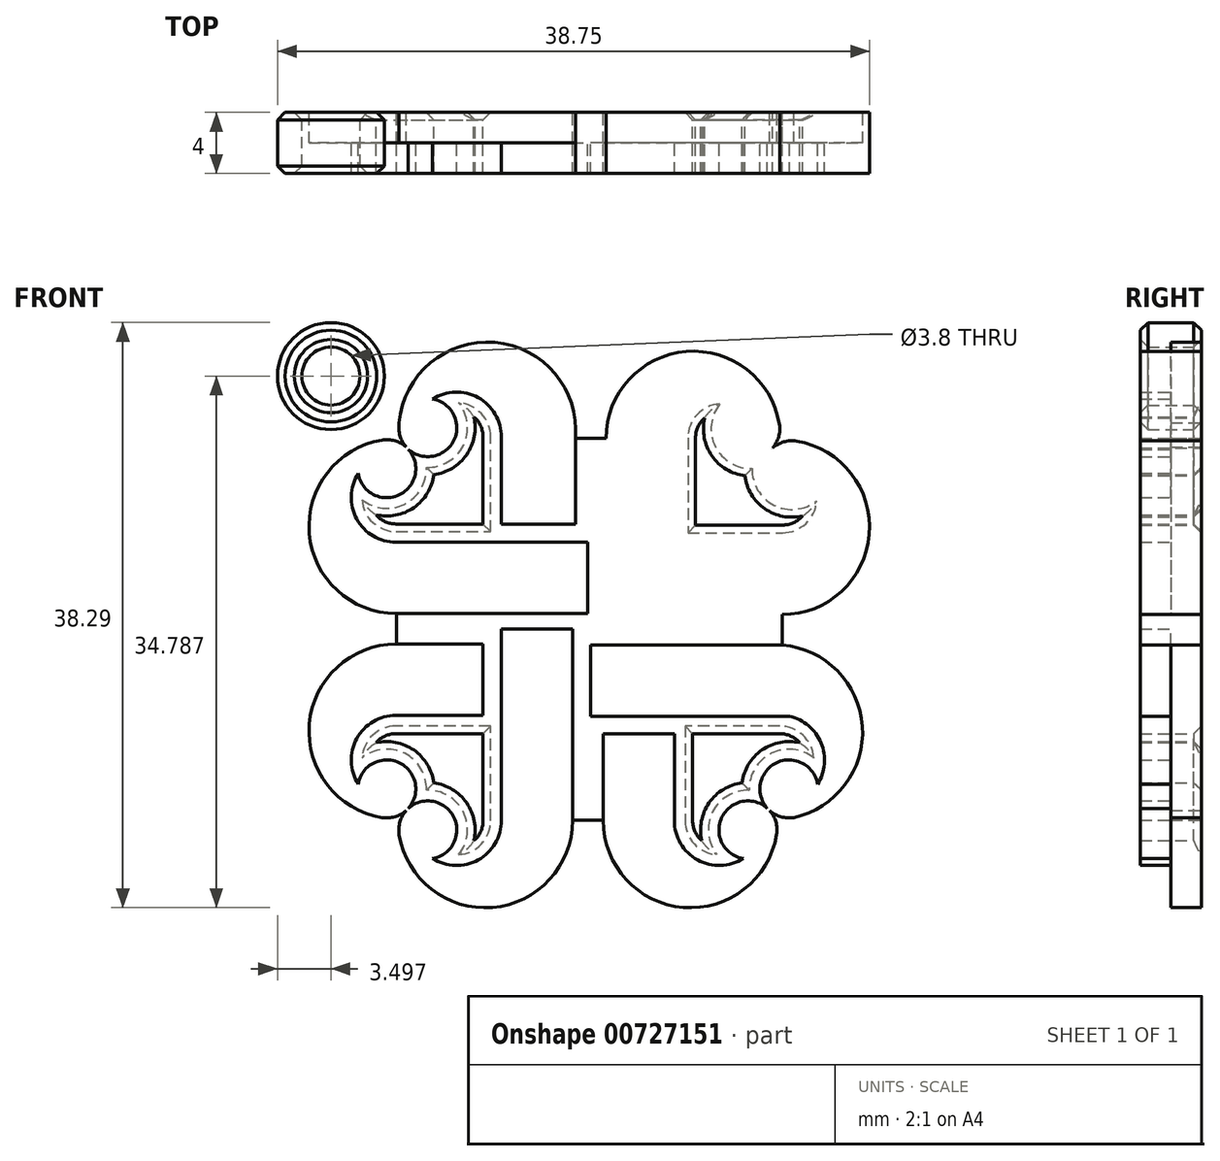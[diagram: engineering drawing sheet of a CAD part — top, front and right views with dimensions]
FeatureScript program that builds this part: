
annotation { "Feature Type Name" : "Feature", "Feature Type Description" : "" }
export const myFeature = defineFeature(function(context is Context, id is Id, definition is map)
    precondition{}
    {
        {
            var Q0;
            Q0=qCreatedBy(makeId("Front.planeOp"),FACE);
            var sketch = newSketch(context, id + "F0", { "sketchPlane" : qUnion([Q0])});
            skPoint(sketch, "E0.middle", {"position": v(0, 0) * mm});
            skLineSegment(sketch, "E1.0", {"start": v(1.19, 12.45) * mm, "end": v(1.19, 0.91) * mm});
            skLineSegment(sketch, "E2.MirrorCS", {"start": v(5.84, 12.48) * mm, "end": v(5.84, -0.09) * mm});
            skArc(sketch, "E3.MirrorCS", {"start": v(5.84, 12.48) * mm, "mid": v(7.36, 15.05) * mm, "end": v(10.35, 14.96) * mm});
            skArc(sketch, "E4.MirrorCS", {"start": v(12.53, 13.4) * mm, "mid": v(12.48, 12.56) * mm, "end": v(12.07, 11.82) * mm});
            skArc(sketch, "E5.MirrorCS", {"start": v(1.19, 12.45) * mm, "mid": v(6.43, 18.14) * mm, "end": v(12.53, 13.4) * mm});
            skPoint(sketch, "E6.MirrorP", {"position": v(8.93, 15.5) * mm});
            skPoint(sketch, "E7.MirrorP", {"position": v(12.53, 13.4) * mm});
            skPoint(sketch, "E8.MirrorP", {"position": v(10.35, 14.96) * mm});
            skLineSegment(sketch, "E9.0", {"start": v(7.04, 12.48) * mm, "end": v(7.04, 6.79) * mm});
            skArc(sketch, "E9.1", {"start": v(7.04, 12.48) * mm, "mid": v(7.2, 13.2) * mm, "end": v(7.64, 13.8) * mm});
            skArc(sketch, "E9.3", {"start": v(1.1, 16.21) * mm, "mid": v(8.05, 19.27) * mm, "end": v(13.61, 14.1) * mm});
            skLineSegment(sketch, "E10.MirrorCS", {"start": v(12.72, 0.93) * mm, "end": v(7.04, 0.93) * mm});
            skLineSegment(sketch, "E11.MirrorCS", {"start": v(12.74, 5.59) * mm, "end": v(7.04, 5.59) * mm});
            skLineSegment(sketch, "E12.MirrorCS", {"start": v(12.74, 6.79) * mm, "end": v(7.04, 6.79) * mm});
            skPoint(sketch, "E13.MirrorP", {"position": v(15.5, 8.93) * mm});
            skPoint(sketch, "E14.MirrorP", {"position": v(15.22, 10.1) * mm});
            skArc(sketch, "E15.MirrorCS", {"start": v(12.72, 0.93) * mm, "mid": v(18.42, 6.17) * mm, "end": v(13.66, 12.28) * mm});
            skArc(sketch, "E16.MirrorCS", {"start": v(12.74, 5.59) * mm, "mid": v(15.31, 7.1) * mm, "end": v(15.22, 10.1) * mm});
            skArc(sketch, "E17.MirrorCS", {"start": v(12.74, 6.79) * mm, "mid": v(13.46, 6.94) * mm, "end": v(14.05, 7.39) * mm});
            skPoint(sketch, "E18.MirrorP", {"position": v(13.66, 12.28) * mm});
            skArc(sketch, "E19.MirrorCS", {"start": v(16.38, 0.78) * mm, "mid": v(19.55, 7.74) * mm, "end": v(14.35, 13.36) * mm});
            skArc(sketch, "E20.MirrorCS", {"start": v(13.66, 12.28) * mm, "mid": v(12.81, 12.23) * mm, "end": v(12.08, 11.82) * mm});
            skArc(sketch, "E21.trimOffspring", {"start": v(10.27, 10.02) * mm, "mid": v(8.12, 11.32) * mm, "end": v(7.64, 13.8) * mm});
            skArc(sketch, "E22.trimOffspring", {"start": v(10.27, 10.02) * mm, "mid": v(11.58, 7.86) * mm, "end": v(14.05, 7.39) * mm});
            skLineSegment(sketch, "E23.1.0", {"start": v(-12.55, 5.66) * mm, "end": v(0, 5.66) * mm});
            skArc(sketch, "E23.1.1", {"start": v(-13.47, 12.35) * mm, "mid": v(-12.63, 12.3) * mm, "end": v(-11.9, 11.89) * mm});
            skPoint(sketch, "E23.1.2", {"position": v(-13.47, 12.35) * mm});
            skArc(sketch, "E23.1.3", {"start": v(-10.09, 10.09) * mm, "mid": v(-7.93, 11.4) * mm, "end": v(-7.46, 13.87) * mm});
            skPoint(sketch, "E23.1.4", {"position": v(-15.03, 10.17) * mm});
            skLineSegment(sketch, "E23.1.5", {"start": v(-6.86, 12.55) * mm, "end": v(-6.86, 6.86) * mm});
            skArc(sketch, "E23.1.6", {"start": v(-0.6, 16.26) * mm, "mid": v(-7.9, 19.82) * mm, "end": v(-13.84, 14.32) * mm});
            skArc(sketch, "E23.1.7", {"start": v(-0.81, 12.47) * mm, "mid": v(-6.08, 18.74) * mm, "end": v(-12.35, 13.47) * mm});
            skLineSegment(sketch, "E23.1.9", {"start": v(-5.66, 12.55) * mm, "end": v(-5.66, 6.86) * mm});
            skPoint(sketch, "E23.1.10", {"position": v(-15.5, 8.93) * mm});
            skArc(sketch, "E23.1.11", {"start": v(-12.54, 1) * mm, "mid": v(-18.23, 6.24) * mm, "end": v(-13.47, 12.35) * mm});
            skArc(sketch, "E23.1.12", {"start": v(-10.09, 10.09) * mm, "mid": v(-11.4, 7.93) * mm, "end": v(-13.87, 7.46) * mm});
            skArc(sketch, "E23.1.13", {"start": v(-12.35, 13.47) * mm, "mid": v(-12.3, 12.63) * mm, "end": v(-11.89, 11.9) * mm});
            skArc(sketch, "E23.1.14", {"start": v(-16.76, 0.1) * mm, "mid": v(-20.22, 7.56) * mm, "end": v(-14.6, 13.56) * mm});
            skLineSegment(sketch, "E23.1.15", {"start": v(-12.54, 1) * mm, "end": v(-1, 1) * mm});
            skLineSegment(sketch, "E23.1.16", {"start": v(-0.81, 12.47) * mm, "end": v(-0.81, 6.86) * mm});
            skPoint(sketch, "E23.1.17", {"position": v(-8.93, 15.5) * mm});
            skPoint(sketch, "E23.1.18", {"position": v(-10.17, 15.03) * mm});
            skPoint(sketch, "E23.1.19", {"position": v(-12.35, 13.47) * mm});
            skArc(sketch, "E23.1.20", {"start": v(-12.55, 5.66) * mm, "mid": v(-15.12, 7.18) * mm, "end": v(-15.03, 10.17) * mm});
            skArc(sketch, "E23.1.21", {"start": v(-12.55, 6.86) * mm, "mid": v(-13.27, 7.02) * mm, "end": v(-13.87, 7.46) * mm});
            skLineSegment(sketch, "E23.1.22", {"start": v(-12.55, 6.86) * mm, "end": v(-6.86, 6.86) * mm});
            skArc(sketch, "E23.1.23", {"start": v(-6.86, 12.55) * mm, "mid": v(-7.02, 13.27) * mm, "end": v(-7.46, 13.87) * mm});
            skArc(sketch, "E23.1.24", {"start": v(-5.66, 12.55) * mm, "mid": v(-7.18, 15.12) * mm, "end": v(-10.17, 15.03) * mm});
            skLineSegment(sketch, "E23.1.25", {"start": v(-12.54, 1) * mm, "end": v(-1, 1) * mm});
            skLineSegment(sketch, "E23.2.0", {"start": v(-5.66, -12.55) * mm, "end": v(-5.66, 0) * mm});
            skArc(sketch, "E23.2.1", {"start": v(-12.35, -13.47) * mm, "mid": v(-12.3, -12.63) * mm, "end": v(-11.89, -11.9) * mm});
            skPoint(sketch, "E23.2.2", {"position": v(-12.35, -13.47) * mm});
            skArc(sketch, "E23.2.3", {"start": v(-10.09, -10.09) * mm, "mid": v(-11.4, -7.93) * mm, "end": v(-13.87, -7.46) * mm});
            skPoint(sketch, "E23.2.4", {"position": v(-10.17, -15.03) * mm});
            skLineSegment(sketch, "E23.2.5", {"start": v(-12.55, -6.86) * mm, "end": v(-6.86, -6.86) * mm});
            skArc(sketch, "E23.2.6", {"start": v(-16.72, -1.58) * mm, "mid": v(-19.62, -8.36) * mm, "end": v(-14.59, -13.75) * mm});
            skArc(sketch, "E23.2.7", {"start": v(-12.54, -1) * mm, "mid": v(-18.23, -6.24) * mm, "end": v(-13.47, -12.35) * mm});
            skLineSegment(sketch, "E23.2.9", {"start": v(-12.55, -5.66) * mm, "end": v(-6.86, -5.66) * mm});
            skPoint(sketch, "E23.2.10", {"position": v(-8.93, -15.5) * mm});
            skArc(sketch, "E23.2.11", {"start": v(-1, -12.54) * mm, "mid": v(-6.24, -18.23) * mm, "end": v(-12.35, -13.47) * mm});
            skArc(sketch, "E23.2.12", {"start": v(-10.09, -10.09) * mm, "mid": v(-7.93, -11.4) * mm, "end": v(-7.46, -13.87) * mm});
            skArc(sketch, "E23.2.13", {"start": v(-13.47, -12.35) * mm, "mid": v(-12.63, -12.3) * mm, "end": v(-11.9, -11.89) * mm});
            skArc(sketch, "E23.2.14", {"start": v(-1.27, -16.52) * mm, "mid": v(-8.24, -19.68) * mm, "end": v(-13.85, -14.49) * mm});
            skLineSegment(sketch, "E23.2.15", {"start": v(-1, -12.54) * mm, "end": v(-1, -1) * mm});
            skLineSegment(sketch, "E23.2.16", {"start": v(-12.54, -1) * mm, "end": v(-6.86, -1) * mm});
            skPoint(sketch, "E23.2.17", {"position": v(-15.5, -8.93) * mm});
            skPoint(sketch, "E23.2.18", {"position": v(-15.03, -10.17) * mm});
            skPoint(sketch, "E23.2.19", {"position": v(-13.47, -12.35) * mm});
            skArc(sketch, "E23.2.20", {"start": v(-5.66, -12.55) * mm, "mid": v(-7.18, -15.12) * mm, "end": v(-10.17, -15.03) * mm});
            skArc(sketch, "E23.2.21", {"start": v(-6.86, -12.55) * mm, "mid": v(-7.02, -13.27) * mm, "end": v(-7.46, -13.87) * mm});
            skLineSegment(sketch, "E23.2.22", {"start": v(-6.86, -12.55) * mm, "end": v(-6.86, -6.86) * mm});
            skArc(sketch, "E23.2.23", {"start": v(-12.55, -6.86) * mm, "mid": v(-13.27, -7.02) * mm, "end": v(-13.87, -7.46) * mm});
            skArc(sketch, "E23.2.24", {"start": v(-12.55, -5.66) * mm, "mid": v(-15.12, -7.18) * mm, "end": v(-15.03, -10.17) * mm});
            skLineSegment(sketch, "E23.2.25", {"start": v(-1, -12.54) * mm, "end": v(-1, -1) * mm});
            skLineSegment(sketch, "E23.3.0", {"start": v(13.2, -5.73) * mm, "end": v(0.19, -5.73) * mm});
            skArc(sketch, "E23.3.1", {"start": v(13.47, -12.35) * mm, "mid": v(12.63, -12.3) * mm, "end": v(11.9, -11.89) * mm});
            skPoint(sketch, "E23.3.2", {"position": v(13.47, -12.35) * mm});
            skArc(sketch, "E23.3.3", {"start": v(10.09, -10.09) * mm, "mid": v(7.93, -11.4) * mm, "end": v(7.46, -13.87) * mm});
            skPoint(sketch, "E23.3.4", {"position": v(15.03, -10.17) * mm});
            skLineSegment(sketch, "E23.3.5", {"start": v(6.86, -12.55) * mm, "end": v(6.86, -6.86) * mm});
            skArc(sketch, "E23.3.6", {"start": v(0.42, -16.52) * mm, "mid": v(7.45, -19.67) * mm, "end": v(13.03, -14.37) * mm});
            skArc(sketch, "E23.3.7", {"start": v(1, -12.54) * mm, "mid": v(6.24, -18.23) * mm, "end": v(12.35, -13.47) * mm});
            skLineSegment(sketch, "E23.3.9", {"start": v(5.66, -12.55) * mm, "end": v(5.66, -6.86) * mm});
            skPoint(sketch, "E23.3.10", {"position": v(15.5, -8.93) * mm});
            skArc(sketch, "E23.3.11", {"start": v(12.72, -1.07) * mm, "mid": v(17.96, -6.39) * mm, "end": v(13.47, -12.35) * mm});
            skArc(sketch, "E23.3.12", {"start": v(10.09, -10.09) * mm, "mid": v(11.4, -7.93) * mm, "end": v(13.87, -7.46) * mm});
            skArc(sketch, "E23.3.13", {"start": v(12.35, -13.47) * mm, "mid": v(12.3, -12.63) * mm, "end": v(11.89, -11.9) * mm});
            skArc(sketch, "E23.3.14", {"start": v(16.38, -0.92) * mm, "mid": v(19.5, -8.14) * mm, "end": v(13.85, -13.6) * mm});
            skLineSegment(sketch, "E23.3.15", {"start": v(12.72, -1.07) * mm, "end": v(1.19, -1.07) * mm});
            skLineSegment(sketch, "E23.3.16", {"start": v(1, -12.54) * mm, "end": v(1, -6.86) * mm});
            skPoint(sketch, "E23.3.17", {"position": v(8.93, -15.5) * mm});
            skPoint(sketch, "E23.3.18", {"position": v(10.17, -15.03) * mm});
            skPoint(sketch, "E23.3.19", {"position": v(12.35, -13.47) * mm});
            skArc(sketch, "E23.3.20", {"start": v(13.2, -5.73) * mm, "mid": v(15.26, -7.47) * mm, "end": v(15.03, -10.17) * mm});
            skArc(sketch, "E23.3.21", {"start": v(12.55, -6.86) * mm, "mid": v(13.27, -7.02) * mm, "end": v(13.87, -7.46) * mm});
            skLineSegment(sketch, "E23.3.22", {"start": v(12.55, -6.86) * mm, "end": v(6.86, -6.86) * mm});
            skArc(sketch, "E23.3.23", {"start": v(6.86, -12.55) * mm, "mid": v(7.02, -13.27) * mm, "end": v(7.46, -13.87) * mm});
            skArc(sketch, "E23.3.24", {"start": v(5.66, -12.55) * mm, "mid": v(7.18, -15.12) * mm, "end": v(10.17, -15.03) * mm});
            skLineSegment(sketch, "E23.3.25", {"start": v(12.72, -1.07) * mm, "end": v(1.19, -1.07) * mm});
            skLineSegment(sketch, "E24", {"start": v(5.84, -0.09) * mm, "end": v(1.19, -0.09) * mm});
            skLineSegment(sketch, "E25", {"start": v(0, 5.66) * mm, "end": v(0, 1) * mm});
            skLineSegment(sketch, "E26", {"start": v(-5.66, 0) * mm, "end": v(-1, 0) * mm});
            skLineSegment(sketch, "E27", {"start": v(0.19, -5.73) * mm, "end": v(0.19, -1.07) * mm});
            skLineSegment(sketch, "E28", {"start": v(1.19, 0.91) * mm, "end": v(1.19, -0.09) * mm});
            skLineSegment(sketch, "E29", {"start": v(-1, 1) * mm, "end": v(0, 1) * mm});
            skLineSegment(sketch, "E30", {"start": v(-1, -1) * mm, "end": v(-1, 0) * mm});
            skLineSegment(sketch, "E31", {"start": v(1.19, -1.07) * mm, "end": v(0.19, -1.07) * mm});
            skLineSegment(sketch, "E32.trimOffspring", {"start": v(7.04, 5.59) * mm, "end": v(7.04, 0.93) * mm});
            skLineSegment(sketch, "E33.trimOffspring", {"start": v(-5.66, 6.86) * mm, "end": v(-0.81, 6.86) * mm});
            skLineSegment(sketch, "E34.trimOffspring", {"start": v(-6.86, -5.66) * mm, "end": v(-6.86, -1) * mm});
            skLineSegment(sketch, "E35.trimOffspring", {"start": v(5.66, -6.86) * mm, "end": v(1, -6.86) * mm});
            skPoint(sketch, "E36", {"position": v(-11.82, -11.82) * mm});
            skPoint(sketch, "E37", {"position": v(-11.82, 11.82) * mm});
            skPoint(sketch, "E38", {"position": v(11.82, -11.82) * mm});
            skPoint(sketch, "E39", {"position": v(12, 11.75) * mm});
            skLineSegment(sketch, "E40", {"start": v(12.72, 0.93) * mm, "end": v(12.72, -1.07) * mm});
            skLineSegment(sketch, "E41", {"start": v(1, -12.54) * mm, "end": v(-1, -12.54) * mm});
            skLineSegment(sketch, "E42", {"start": v(-12.54, -1) * mm, "end": v(-12.54, 1) * mm});
            skLineSegment(sketch, "E43", {"start": v(-0.81, 12.47) * mm, "end": v(1.19, 12.45) * mm});
            skPoint(sketch, "E44.visualSharp", {"position": v(14.37, -0.07) * mm});
            skArc(sketch, "E44.filletArc", {"start": v(16.38, 0.78) * mm, "mid": v(15.91, -0.07) * mm, "end": v(16.38, -0.92) * mm});
            skPoint(sketch, "E45.visualSharp", {"position": v(0.19, 14.1) * mm});
            skArc(sketch, "E45.filletArc", {"start": v(-0.6, 16.26) * mm, "mid": v(0.23, 15.75) * mm, "end": v(1.1, 16.21) * mm});
            skPoint(sketch, "E46.visualSharp", {"position": v(-14.85, -0.7) * mm});
            skArc(sketch, "E46.filletArc", {"start": v(-16.72, -1.58) * mm, "mid": v(-16.28, -0.73) * mm, "end": v(-16.76, 0.1) * mm});
            skPoint(sketch, "E47.visualSharp", {"position": v(-0.42, -14.5) * mm});
            skArc(sketch, "E47.filletArc", {"start": v(0.42, -16.52) * mm, "mid": v(-0.42, -16.05) * mm, "end": v(-1.27, -16.52) * mm});
            skArc(sketch, "E48.filletArc", {"start": v(-13.85, -14.49) * mm, "mid": v(-14.12, -14.02) * mm, "end": v(-14.59, -13.75) * mm});
            skArc(sketch, "E49.filletArc", {"start": v(13.85, -13.6) * mm, "mid": v(13.32, -13.86) * mm, "end": v(13.03, -14.37) * mm});
            skArc(sketch, "E50.filletArc", {"start": v(13.61, 14.1) * mm, "mid": v(13.88, 13.62) * mm, "end": v(14.35, 13.36) * mm});
            skArc(sketch, "E51.filletArc", {"start": v(-14.6, 13.56) * mm, "mid": v(-14.1, 13.83) * mm, "end": v(-13.84, 14.32) * mm});
            skArc(sketch, "E52", {"start": v(11.93, 11.68) * mm, "mid": v(11.93, 11.68) * mm, "end": v(11.93, 11.67) * mm});
            skArc(sketch, "E53.trimOffspring", {"start": v(12.08, 11.82) * mm, "mid": v(12.07, 11.82) * mm, "end": v(12.07, 11.82) * mm});
            skArc(sketch, "E54.trimOffspring", {"start": v(11.93, 11.67) * mm, "mid": v(12.52, 8.7) * mm, "end": v(15.22, 10.1) * mm});
            skArc(sketch, "E55.trimOffspring", {"start": v(11.93, 11.68) * mm, "mid": v(8.95, 12.27) * mm, "end": v(10.35, 14.96) * mm});
            skArc(sketch, "E56", {"start": v(-11.89, 11.9) * mm, "mid": v(-11.89, 11.89) * mm, "end": v(-11.9, 11.89) * mm});
            skArc(sketch, "E57.trimOffspring", {"start": v(-11.75, 11.75) * mm, "mid": v(-11.75, 11.75) * mm, "end": v(-11.75, 11.75) * mm});
            skArc(sketch, "E58.trimOffspring", {"start": v(-11.75, 11.75) * mm, "mid": v(-8.76, 12.34) * mm, "end": v(-10.17, 15.03) * mm});
            skArc(sketch, "E59.trimOffspring", {"start": v(-11.75, 11.75) * mm, "mid": v(-12.34, 8.76) * mm, "end": v(-15.03, 10.17) * mm});
            skArc(sketch, "E60", {"start": v(-11.9, -11.89) * mm, "mid": v(-11.89, -11.89) * mm, "end": v(-11.89, -11.9) * mm});
            skArc(sketch, "E61.trimOffspring", {"start": v(-11.75, -11.75) * mm, "mid": v(-11.75, -11.75) * mm, "end": v(-11.75, -11.75) * mm});
            skArc(sketch, "E62.trimOffspring", {"start": v(-11.75, -11.75) * mm, "mid": v(-8.76, -12.34) * mm, "end": v(-10.17, -15.03) * mm});
            skArc(sketch, "E63.trimOffspring", {"start": v(-11.75, -11.75) * mm, "mid": v(-12.34, -8.76) * mm, "end": v(-15.03, -10.17) * mm});
            skArc(sketch, "E64", {"start": v(11.75, -11.75) * mm, "mid": v(11.75, -11.75) * mm, "end": v(11.75, -11.75) * mm});
            skArc(sketch, "E65.trimOffspring", {"start": v(11.89, -11.9) * mm, "mid": v(11.89, -11.89) * mm, "end": v(11.9, -11.89) * mm});
            skArc(sketch, "E66.trimOffspring", {"start": v(11.75, -11.75) * mm, "mid": v(8.76, -12.34) * mm, "end": v(10.17, -15.03) * mm});
            skArc(sketch, "E67.trimOffspring", {"start": v(11.75, -11.75) * mm, "mid": v(12.34, -8.76) * mm, "end": v(15.03, -10.17) * mm});
            skCircle(sketch, "E68", {"center": v(-16.81, 16.54) * mm, "radius": 3.5 * mm});
            skPoint(sketch, "E68.first.point", {"position": v(-15.57, 13.26) * mm});
            skPoint(sketch, "E68.second.point", {"position": v(-13.54, 15.29) * mm});
            skPoint(sketch, "E68.third.point", {"position": v(-17.12, 13.05) * mm});
            skCircle(sketch, "E69.0", {"center": v(-16.81, 16.54) * mm, "radius": 1.9 * mm});
            skSolve(sketch);
        }
        {
            var Q0;
            Q0=makeQuery(id+"F0.imprint","IMPRINT",FACE,{"disambiguationData":[TD([[makeQuery(id+"F0.imprint","IMPRINT",EDGE,{"derivedFrom":sQuery(id+"F0.wireOp",EDGE,"E4.MirrorCS")}),1.0]])]});
            extrude(context, id + "F1", {"entities" : qUnion([Q0]), "depth" : 4 * mm, "offsetDistance" : 25 * mm});
        }
        {
            var Q0;
            Q0=makeQuery(id+"F0.imprint","IMPRINT",FACE,{"disambiguationData":[TD([[makeQuery(id+"F0.imprint","IMPRINT",EDGE,{"derivedFrom":sQuery(id+"F0.wireOp",EDGE,"E2.MirrorCS")}),1.0]])]});
            extrude(context, id + "F2", {"entities" : qUnion([Q0]), "operationType" : NewBodyOperationType.ADD, "depth" : 4 * mm, "offsetDistance" : 25 * mm});
        }
        {
            var Q0;
            Q0=makeQuery(id+"F0.imprint","IMPRINT",FACE,{"disambiguationData":[TD([[makeQuery(id+"F0.imprint","IMPRINT",EDGE,{"derivedFrom":sQuery(id+"F0.wireOp",EDGE,"E69.0")}),-1.0]])]});
            extrude(context, id + "F3", {"entities" : qUnion([Q0]), "operationType" : NewBodyOperationType.ADD, "depth" : 4 * mm, "offsetDistance" : 25 * mm});
        }
        {
            var Q0;
            Q0=makeQuery(id+"F0.imprint","IMPRINT",FACE,{"disambiguationData":[TD([[makeQuery(id+"F0.imprint","IMPRINT",EDGE,{"derivedFrom":sQuery(id+"F0.wireOp",EDGE,"E23.3.0")}),-1.0]])]});
            var Q1;
            Q1=makeQuery(id+"F0.imprint","IMPRINT",FACE,{"disambiguationData":[TD([[makeQuery(id+"F0.imprint","IMPRINT",EDGE,{"derivedFrom":sQuery(id+"F0.wireOp",EDGE,"E23.2.0")}),-1.0]])]});
            var Q2;
            Q2=makeQuery(id+"F0.imprint","IMPRINT",FACE,{"disambiguationData":[TD([[makeQuery(id+"F0.imprint","IMPRINT",EDGE,{"derivedFrom":sQuery(id+"F0.wireOp",EDGE,"E23.1.0")}),-1.0]])]});
            var Q3;
            Q3=makeQuery(id+"F0.imprint","IMPRINT",FACE,{"disambiguationData":[TD([[makeQuery(id+"F0.imprint","IMPRINT",EDGE,{"derivedFrom":sQuery(id+"F0.wireOp",EDGE,"E2.MirrorCS")}),-1.0]])]});
            extrude(context, id + "F4", {"entities" : qUnion([Q0, Q1, Q2, Q3]), "operationType" : NewBodyOperationType.ADD, "depth" : 2 * mm, "offsetDistance" : 25 * mm});
        }
        {
            var Q0;
            Q0=makeQuery(id+"F3.opExtrude","CAP_EDGE",EDGE,{"disambiguationData":[OSD([sQuery(id+"F0.wireOp",EDGE,"E68")])],"isStart":false});
            var Q1;
            Q1=makeQuery(id+"F3.opExtrude","CAP_EDGE",EDGE,{"disambiguationData":[OSD([sQuery(id+"F0.wireOp",EDGE,"E69.0")])],"isStart":false});
            var Q2;
            Q2=makeQuery(id+"F3.opExtrude","CAP_EDGE",EDGE,{"disambiguationData":[OSD([sQuery(id+"F0.wireOp",EDGE,"E68")])],"isStart":true});
            var Q3;
            Q3=makeQuery(id+"F3.opExtrude","CAP_EDGE",EDGE,{"disambiguationData":[OSD([sQuery(id+"F0.wireOp",EDGE,"E69.0")])],"isStart":true});
            var Q4;
            Q4=makeQuery(id+"F1.opExtrude","CAP_EDGE",EDGE,{"disambiguationData":[OSD([sQuery(id+"F0.wireOp",EDGE,"E23.1.14")])],"isStart":true});
            var Q5;
            Q5=makeQuery(id+"F2.opExtrude","CAP_EDGE",EDGE,{"disambiguationData":[OSD([sQuery(id+"F0.wireOp",EDGE,"E23.1.22")])],"isStart":true});
            var Q6;
            Q6=makeQuery(id+"F2.opExtrude","CAP_EDGE",EDGE,{"disambiguationData":[OSD([sQuery(id+"F0.wireOp",EDGE,"E23.1.12")])],"isStart":true});
            var Q7;
            Q7=makeQuery(id+"F2.opExtrude","CAP_EDGE",EDGE,{"disambiguationData":[OSD([sQuery(id+"F0.wireOp",EDGE,"E23.1.3")])],"isStart":true});
            var Q8;
            Q8=makeQuery(id+"F2.opExtrude","CAP_EDGE",EDGE,{"disambiguationData":[OSD([sQuery(id+"F0.wireOp",EDGE,"E23.1.5")])],"isStart":true});
            var Q9;
            Q9=makeQuery(id+"F2.opExtrude","CAP_EDGE",EDGE,{"disambiguationData":[OSD([sQuery(id+"F0.wireOp",EDGE,"E23.1.23")])],"isStart":true});
            var Q10;
            Q10=makeQuery(id+"F2.opExtrude","CAP_EDGE",EDGE,{"disambiguationData":[OSD([sQuery(id+"F0.wireOp",EDGE,"E23.1.21")])],"isStart":true});
            var Q11;
            Q11=makeQuery(id+"F2.opExtrude","CAP_EDGE",EDGE,{"disambiguationData":[OSD([sQuery(id+"F0.wireOp",EDGE,"E22.trimOffspring")])],"isStart":true});
            var Q12;
            Q12=makeQuery(id+"F2.opExtrude","CAP_EDGE",EDGE,{"disambiguationData":[OSD([sQuery(id+"F0.wireOp",EDGE,"E21.trimOffspring")])],"isStart":true});
            var Q13;
            Q13=makeQuery(id+"F2.opExtrude","CAP_EDGE",EDGE,{"disambiguationData":[OSD([sQuery(id+"F0.wireOp",EDGE,"E9.1")])],"isStart":true});
            var Q14;
            Q14=makeQuery(id+"F2.opExtrude","CAP_EDGE",EDGE,{"disambiguationData":[OSD([sQuery(id+"F0.wireOp",EDGE,"E9.0")])],"isStart":true});
            var Q15;
            Q15=makeQuery(id+"F2.opExtrude","CAP_EDGE",EDGE,{"disambiguationData":[OSD([sQuery(id+"F0.wireOp",EDGE,"E12.MirrorCS")])],"isStart":true});
            var Q16;
            Q16=makeQuery(id+"F2.opExtrude","CAP_EDGE",EDGE,{"disambiguationData":[OSD([sQuery(id+"F0.wireOp",EDGE,"E17.MirrorCS")])],"isStart":true});
            var Q17;
            Q17=makeQuery(id+"F2.opExtrude","CAP_EDGE",EDGE,{"disambiguationData":[OSD([sQuery(id+"F0.wireOp",EDGE,"E23.3.22")])],"isStart":true});
            var Q18;
            Q18=makeQuery(id+"F2.opExtrude","CAP_EDGE",EDGE,{"disambiguationData":[OSD([sQuery(id+"F0.wireOp",EDGE,"E23.3.5")])],"isStart":true});
            var Q19;
            Q19=makeQuery(id+"F2.opExtrude","CAP_EDGE",EDGE,{"disambiguationData":[OSD([sQuery(id+"F0.wireOp",EDGE,"E23.3.3")])],"isStart":true});
            var Q20;
            Q20=makeQuery(id+"F2.opExtrude","CAP_EDGE",EDGE,{"disambiguationData":[OSD([sQuery(id+"F0.wireOp",EDGE,"E23.3.23")])],"isStart":true});
            var Q21;
            Q21=makeQuery(id+"F2.opExtrude","CAP_EDGE",EDGE,{"disambiguationData":[OSD([sQuery(id+"F0.wireOp",EDGE,"E23.3.12")])],"isStart":true});
            var Q22;
            Q22=makeQuery(id+"F2.opExtrude","CAP_EDGE",EDGE,{"disambiguationData":[OSD([sQuery(id+"F0.wireOp",EDGE,"E23.3.21")])],"isStart":true});
            var Q23;
            Q23=makeQuery(id+"F2.opExtrude","CAP_EDGE",EDGE,{"disambiguationData":[OSD([sQuery(id+"F0.wireOp",EDGE,"E23.2.5")])],"isStart":true});
            var Q24;
            Q24=makeQuery(id+"F2.opExtrude","CAP_EDGE",EDGE,{"disambiguationData":[OSD([sQuery(id+"F0.wireOp",EDGE,"E23.2.22")])],"isStart":true});
            var Q25;
            Q25=makeQuery(id+"F2.opExtrude","CAP_EDGE",EDGE,{"disambiguationData":[OSD([sQuery(id+"F0.wireOp",EDGE,"E23.2.21")])],"isStart":true});
            var Q26;
            Q26=makeQuery(id+"F2.opExtrude","CAP_EDGE",EDGE,{"disambiguationData":[OSD([sQuery(id+"F0.wireOp",EDGE,"E23.2.12")])],"isStart":true});
            var Q27;
            Q27=makeQuery(id+"F2.opExtrude","CAP_EDGE",EDGE,{"disambiguationData":[OSD([sQuery(id+"F0.wireOp",EDGE,"E23.2.3")])],"isStart":true});
            var Q28;
            Q28=makeQuery(id+"F2.opExtrude","CAP_EDGE",EDGE,{"disambiguationData":[OSD([sQuery(id+"F0.wireOp",EDGE,"E23.2.23")])],"isStart":true});
            chamfer(context, id + "F5", {"entities" : qUnion([Q0, Q1, Q2, Q3, Q4, Q5, Q6, Q7, Q8, Q9, Q10, Q11, Q12, Q13, Q14, Q15, Q16, Q17, Q18, Q19, Q20, Q21, Q22, Q23, Q24, Q25, Q26, Q27, Q28]), "width" : .5 * mm, "tangentPropagation" : true});
        }
    });
